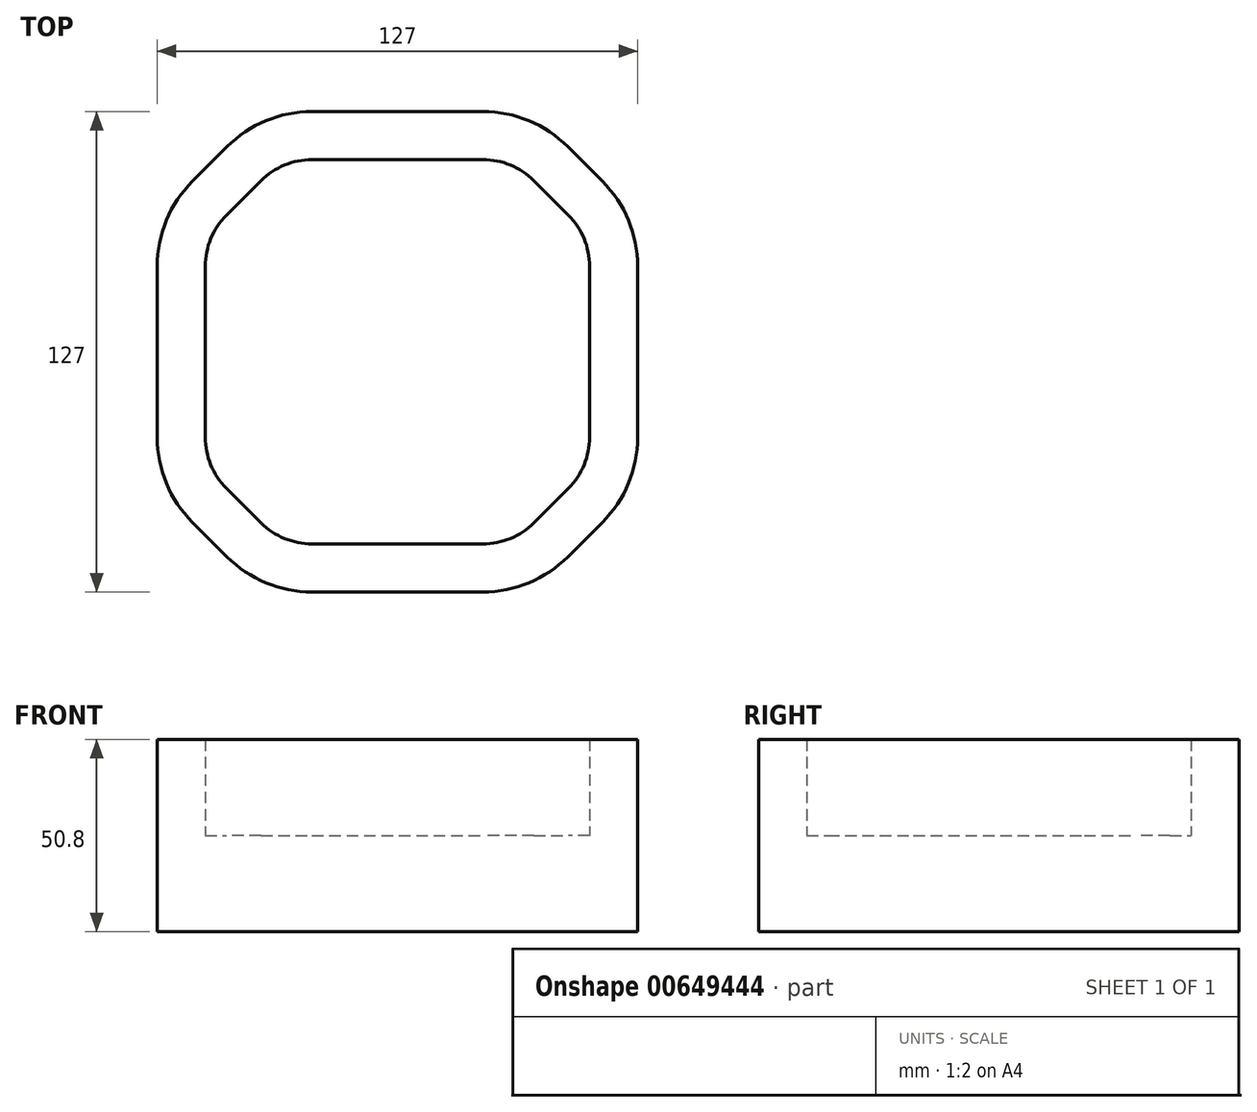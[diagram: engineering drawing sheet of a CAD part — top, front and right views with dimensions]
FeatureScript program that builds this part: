
annotation { "Feature Type Name" : "Feature", "Feature Type Description" : "" }
export const myFeature = defineFeature(function(context is Context, id is Id, definition is map)
    precondition{}
    {
        {
            var Q0;
            Q0=qCreatedBy(makeId("Top.planeOp"),FACE);
            var sketch = newSketch(context, id + "F0", { "sketchPlane" : qUnion([Q0])});
            skLineSegment(sketch, "E0", {"start": v(0, -50.8) * mm, "end": v(22.59, -50.8) * mm});
            skLineSegment(sketch, "E1", {"start": v(36.06, -45.22) * mm, "end": v(45.22, -36.06) * mm});
            skLineSegment(sketch, "E2", {"start": v(50.8, -22.59) * mm, "end": v(50.8, 0) * mm});
            skPoint(sketch, "E3.visualSharp", {"position": v(50.8, -30.48) * mm});
            skArc(sketch, "E3.filletArc", {"start": v(45.22, -36.06) * mm, "mid": v(49.35, -29.88) * mm, "end": v(50.8, -22.59) * mm});
            skPoint(sketch, "E4.visualSharp", {"position": v(30.48, -50.8) * mm});
            skArc(sketch, "E4.filletArc", {"start": v(22.59, -50.8) * mm, "mid": v(29.88, -49.35) * mm, "end": v(36.06, -45.22) * mm});
            skLineSegment(sketch, "E5.0", {"start": v(63.5, -22.59) * mm, "end": v(63.5, 0) * mm});
            skLineSegment(sketch, "E5.1", {"start": v(0, -63.5) * mm, "end": v(22.59, -63.5) * mm});
            skArc(sketch, "E5.2", {"start": v(22.59, -63.5) * mm, "mid": v(34.74, -61.08) * mm, "end": v(45.04, -54.2) * mm});
            skLineSegment(sketch, "E5.3", {"start": v(45.04, -54.2) * mm, "end": v(54.2, -45.04) * mm});
            skArc(sketch, "E5.4", {"start": v(54.2, -45.04) * mm, "mid": v(61.08, -34.74) * mm, "end": v(63.5, -22.59) * mm});
            skLineSegment(sketch, "E6.MirrorCS", {"start": v(0, 50.8) * mm, "end": v(22.59, 50.8) * mm});
            skArc(sketch, "E7.MirrorCS", {"start": v(22.59, 50.8) * mm, "mid": v(29.88, 49.35) * mm, "end": v(36.06, 45.22) * mm});
            skLineSegment(sketch, "E8.MirrorCS", {"start": v(36.06, 45.22) * mm, "end": v(45.22, 36.06) * mm});
            skArc(sketch, "E9.MirrorCS", {"start": v(45.22, 36.06) * mm, "mid": v(49.35, 29.88) * mm, "end": v(50.8, 22.59) * mm});
            skLineSegment(sketch, "E10.MirrorCS", {"start": v(50.8, 22.59) * mm, "end": v(50.8, 0) * mm});
            skLineSegment(sketch, "E11.MirrorCS", {"start": v(0, 63.5) * mm, "end": v(22.59, 63.5) * mm});
            skArc(sketch, "E12.MirrorCS", {"start": v(22.59, 63.5) * mm, "mid": v(34.74, 61.08) * mm, "end": v(45.04, 54.2) * mm});
            skLineSegment(sketch, "E13.MirrorCS", {"start": v(45.04, 54.2) * mm, "end": v(54.2, 45.04) * mm});
            skArc(sketch, "E14.MirrorCS", {"start": v(54.2, 45.04) * mm, "mid": v(61.08, 34.74) * mm, "end": v(63.5, 22.59) * mm});
            skLineSegment(sketch, "E15.MirrorCS", {"start": v(63.5, 22.59) * mm, "end": v(63.5, 0) * mm});
            skArc(sketch, "E16.MirrorCS", {"start": v(-22.59, -50.8) * mm, "mid": v(-29.88, -49.35) * mm, "end": v(-36.06, -45.22) * mm});
            skArc(sketch, "E17.MirrorCS", {"start": v(-45.22, -36.06) * mm, "mid": v(-49.35, -29.88) * mm, "end": v(-50.8, -22.59) * mm});
            skArc(sketch, "E18.MirrorCS", {"start": v(-22.59, 63.5) * mm, "mid": v(-34.74, 61.08) * mm, "end": v(-45.04, 54.2) * mm});
            skLineSegment(sketch, "E19.MirrorCS", {"start": v(-63.5, -22.59) * mm, "end": v(-63.5, 0) * mm});
            skLineSegment(sketch, "E20.MirrorCS", {"start": v(0, -63.5) * mm, "end": v(-22.59, -63.5) * mm});
            skLineSegment(sketch, "E21.MirrorCS", {"start": v(-45.04, -54.2) * mm, "end": v(-54.2, -45.04) * mm});
            skArc(sketch, "E22.MirrorCS", {"start": v(-54.2, 45.04) * mm, "mid": v(-61.08, 34.74) * mm, "end": v(-63.5, 22.59) * mm});
            skLineSegment(sketch, "E23.MirrorCS", {"start": v(0, 50.8) * mm, "end": v(-22.59, 50.8) * mm});
            skLineSegment(sketch, "E24.MirrorCS", {"start": v(-50.8, 22.59) * mm, "end": v(-50.8, 0) * mm});
            skLineSegment(sketch, "E25.MirrorCS", {"start": v(-63.5, 22.59) * mm, "end": v(-63.5, 0) * mm});
            skArc(sketch, "E26.MirrorCS", {"start": v(-54.2, -45.04) * mm, "mid": v(-61.08, -34.74) * mm, "end": v(-63.5, -22.59) * mm});
            skArc(sketch, "E27.MirrorCS", {"start": v(-45.22, 36.06) * mm, "mid": v(-49.35, 29.88) * mm, "end": v(-50.8, 22.59) * mm});
            skLineSegment(sketch, "E28.MirrorCS", {"start": v(0, 63.5) * mm, "end": v(-22.59, 63.5) * mm});
            skLineSegment(sketch, "E29.MirrorCS", {"start": v(-50.8, -22.59) * mm, "end": v(-50.8, 0) * mm});
            skPoint(sketch, "E30.MirrorP", {"position": v(-30.48, -50.8) * mm});
            skPoint(sketch, "E31.MirrorP", {"position": v(-50.8, -30.48) * mm});
            skArc(sketch, "E32.MirrorCS", {"start": v(-22.59, 50.8) * mm, "mid": v(-29.88, 49.35) * mm, "end": v(-36.06, 45.22) * mm});
            skArc(sketch, "E33.MirrorCS", {"start": v(-22.59, -63.5) * mm, "mid": v(-34.74, -61.08) * mm, "end": v(-45.04, -54.2) * mm});
            skLineSegment(sketch, "E34.MirrorCS", {"start": v(-36.06, -45.22) * mm, "end": v(-45.22, -36.06) * mm});
            skLineSegment(sketch, "E35.MirrorCS", {"start": v(-45.04, 54.2) * mm, "end": v(-54.2, 45.04) * mm});
            skLineSegment(sketch, "E36.MirrorCS", {"start": v(-36.06, 45.22) * mm, "end": v(-45.22, 36.06) * mm});
            skLineSegment(sketch, "E37.MirrorCS", {"start": v(0, -50.8) * mm, "end": v(-22.59, -50.8) * mm});
            skSolve(sketch);
        }
        {
            var Q0;
            Q0=makeQuery(id+"F0.imprint","IMPRINT",FACE,{"disambiguationData":[TD([[makeQuery(id+"F0.imprint","IMPRINT",EDGE,{"derivedFrom":sQuery(id+"F0.wireOp",EDGE,"E0")}),1.0]])]});
            extrude(context, id + "F1", {"entities" : qUnion([Q0]), "depth" : 25.4 * mm, "offsetDistance" : 25.4 * mm});
        }
        {
            var Q0;
            Q0 = qSketchRegion(id + "F0", true);
            extrude(context, id + "F2", {"entities" : qUnion([Q0]), "operationType" : NewBodyOperationType.ADD, "depth" : 50.8 * mm, "offsetDistance" : 25.4 * mm});
        }
    });
